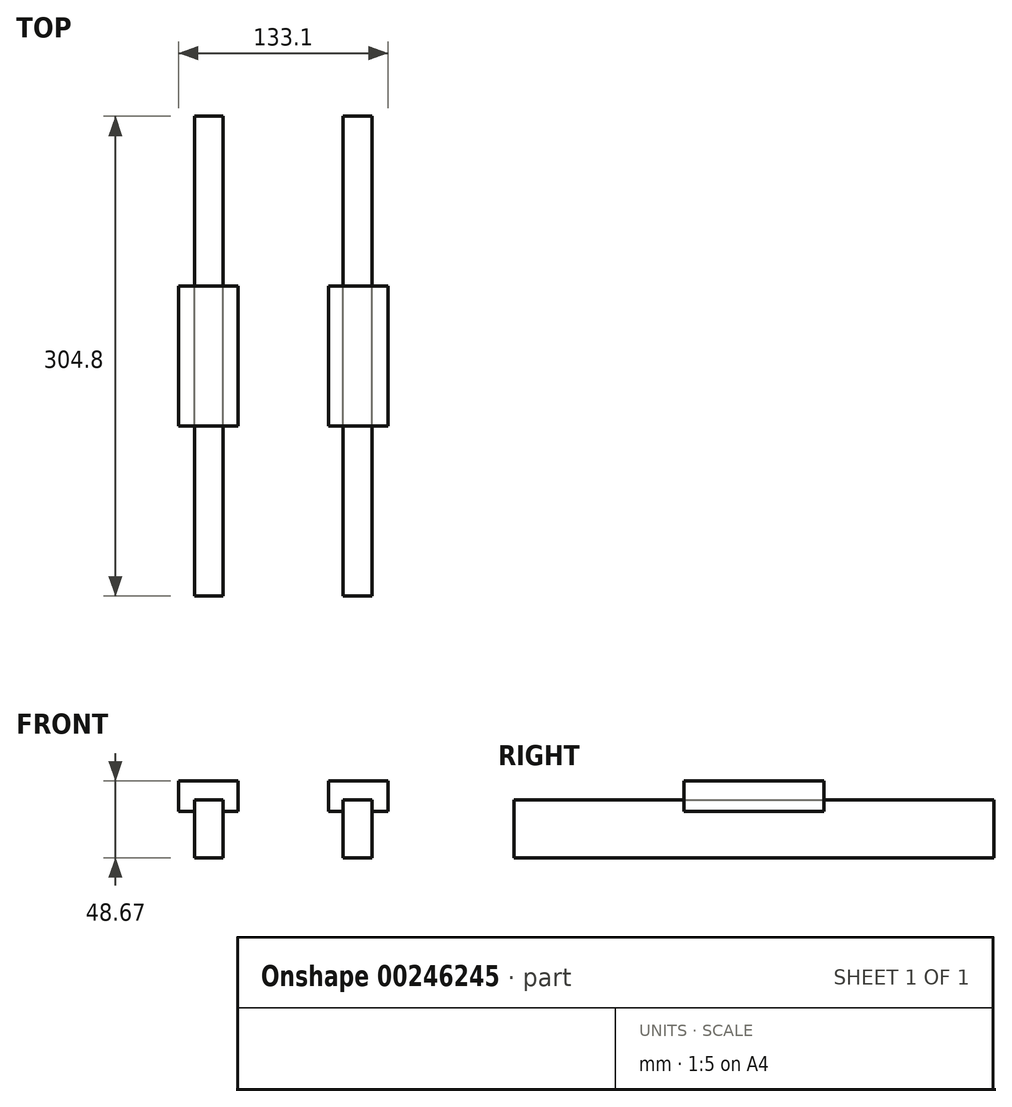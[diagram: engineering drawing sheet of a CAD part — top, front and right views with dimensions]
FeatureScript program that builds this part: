
annotation { "Feature Type Name" : "Feature", "Feature Type Description" : "" }
export const myFeature = defineFeature(function(context is Context, id is Id, definition is map)
    precondition{}
    {
        {
            var Q0;
            Q0=qCreatedBy(makeId("Front.planeOp"),FACE);
            var sketch = newSketch(context, id + "F0", { "sketchPlane" : qUnion([Q0])});
            skLineSegment(sketch, "E0.bottom", {"start": v(-56.39, -36.58) * mm, "end": v(-38.1, -36.58) * mm});
            skLineSegment(sketch, "E0.top", {"start": v(-56.39, 0) * mm, "end": v(-38.1, 0) * mm});
            skLineSegment(sketch, "E0.left", {"start": v(-56.39, -36.58) * mm, "end": v(-56.39, 0) * mm});
            skLineSegment(sketch, "E0.right", {"start": v(-38.1, -36.58) * mm, "end": v(-38.1, 0) * mm});
            skLineSegment(sketch, "E1.bottom", {"start": v(-66.55, 12.1) * mm, "end": v(-28.7, 12.1) * mm});
            skLineSegment(sketch, "E1.top", {"start": v(-66.55, -7.26) * mm, "end": v(-28.7, -7.26) * mm});
            skLineSegment(sketch, "E1.left", {"start": v(-66.55, 12.1) * mm, "end": v(-66.55, -7.26) * mm});
            skLineSegment(sketch, "E1.right", {"start": v(-28.7, 12.1) * mm, "end": v(-28.7, -7.26) * mm});
            skLineSegment(sketch, "E2.MirrorCS", {"start": v(56.39, -36.58) * mm, "end": v(38.1, -36.58) * mm});
            skLineSegment(sketch, "E3.MirrorCS", {"start": v(38.1, -36.58) * mm, "end": v(38.1, 0) * mm});
            skLineSegment(sketch, "E4.MirrorCS", {"start": v(56.39, 0) * mm, "end": v(38.1, 0) * mm});
            skLineSegment(sketch, "E5.MirrorCS", {"start": v(56.39, -36.58) * mm, "end": v(56.39, 0) * mm});
            skLineSegment(sketch, "E6.MirrorCS", {"start": v(66.55, -7.26) * mm, "end": v(28.7, -7.26) * mm});
            skLineSegment(sketch, "E7.MirrorCS", {"start": v(28.7, 12.1) * mm, "end": v(28.7, -7.26) * mm});
            skLineSegment(sketch, "E8.MirrorCS", {"start": v(66.55, 12.1) * mm, "end": v(28.7, 12.1) * mm});
            skLineSegment(sketch, "E9.MirrorCS", {"start": v(66.55, 12.1) * mm, "end": v(66.55, -7.26) * mm});
            skSolve(sketch);
        }
        {
            var Q0;
            {var subQ0=sQuery(id+"F0.wireOp",EDGE,"E0.bottom");Q0=makeQuery(id+"F0.imprint","IMPRINT",FACE,{"disambiguationData":[TD([[makeQuery(id+"F0.imprint","IMPRINT",EDGE,{"derivedFrom":subQ0}),1.0]])]});}
            var Q1;
            {var subQ0=sQuery(id+"F0.wireOp",EDGE,"E0.top");Q1=makeQuery(id+"F0.imprint","IMPRINT",FACE,{"disambiguationData":[TD([[makeQuery(id+"F0.imprint","IMPRINT",EDGE,{"derivedFrom":subQ0}),-1.0]])]});}
            var Q2;
            {var subQ0=sQuery(id+"F0.wireOp",EDGE,"E2.MirrorCS");Q2=makeQuery(id+"F0.imprint","IMPRINT",FACE,{"disambiguationData":[TD([[makeQuery(id+"F0.imprint","IMPRINT",EDGE,{"derivedFrom":subQ0}),-1.0]])]});}
            var Q3;
            {var subQ0=sQuery(id+"F0.wireOp",EDGE,"E4.MirrorCS");Q3=makeQuery(id+"F0.imprint","IMPRINT",FACE,{"disambiguationData":[TD([[makeQuery(id+"F0.imprint","IMPRINT",EDGE,{"derivedFrom":subQ0}),1.0]])]});}
            extrude(context, id + "F1", {"entities" : qUnion([Q0, Q1, Q2, Q3]), "depth" : 152.4 * mm, "hasSecondDirection" : true, "secondDirectionOppositeDirection" : true, "secondDirectionDepth" : 152.4 * mm});
        }
        {
            var Q0;
            {var subQ1=sQuery(id+"F0.wireOp",EDGE,"E0.top");Q0=makeQuery(id+"F0.imprint","IMPRINT",FACE,{"disambiguationData":[TD([[makeQuery(id+"F0.imprint","IMPRINT",EDGE,{"derivedFrom":subQ1}),1.0]])]});}
            var Q1;
            {var subQ4=sQuery(id+"F0.wireOp",EDGE,"E4.MirrorCS");Q1=makeQuery(id+"F0.imprint","IMPRINT",FACE,{"disambiguationData":[TD([[makeQuery(id+"F0.imprint","IMPRINT",EDGE,{"derivedFrom":subQ4}),-1.0]])]});}
            extrude(context, id + "F2", {"entities" : qUnion([Q0, Q1]), "depth" : 44.45 * mm, "hasSecondDirection" : true, "secondDirectionOppositeDirection" : true, "secondDirectionDepth" : 44.45 * mm});
        }
    });
